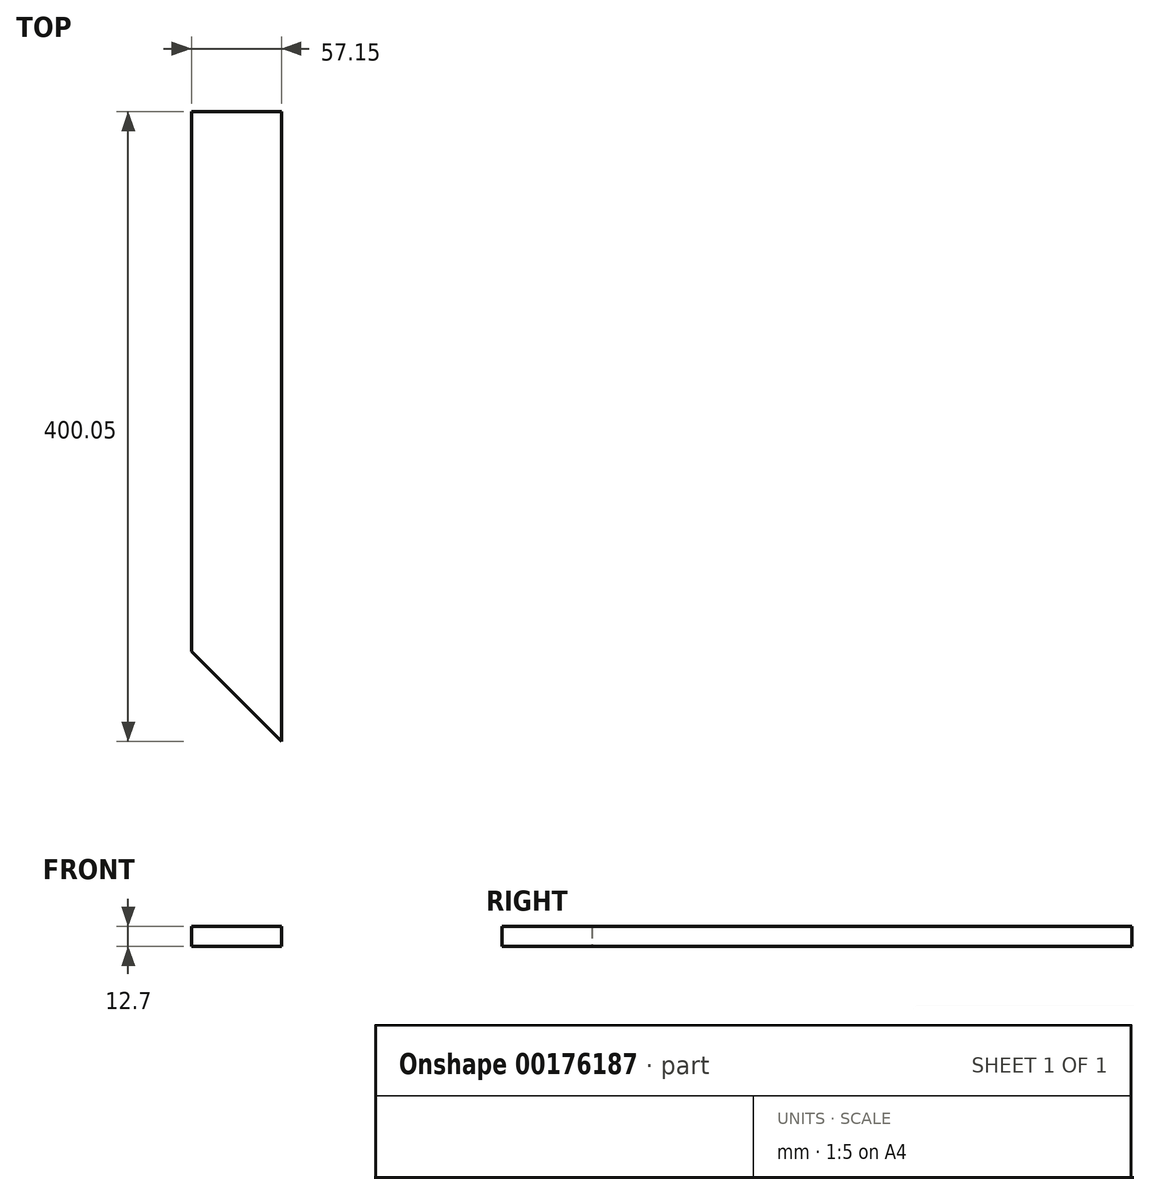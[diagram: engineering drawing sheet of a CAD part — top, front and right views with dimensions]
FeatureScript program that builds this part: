
annotation { "Feature Type Name" : "Feature", "Feature Type Description" : "" }
export const myFeature = defineFeature(function(context is Context, id is Id, definition is map)
    precondition{}
    {
        {
            var Q0;
            Q0=qCreatedBy(makeId("Top.planeOp"),FACE);
            var sketch = newSketch(context, id + "F0", { "sketchPlane" : qUnion([Q0])});
            skLineSegment(sketch, "E0", {"start": v(0, 57.15) * mm, "end": v(0, 400.05) * mm});
            skLineSegment(sketch, "E1", {"start": v(0, 400.05) * mm, "end": v(57.15, 400.05) * mm});
            skLineSegment(sketch, "E2", {"start": v(57.15, 400.05) * mm, "end": v(57.15, 0) * mm});
            skLineSegment(sketch, "E3", {"start": v(57.15, 0) * mm, "end": v(0, 57.15) * mm});
            skSolve(sketch);
        }
        {
            var Q0;
            Q0=makeQuery(id+"F0.imprint","IMPRINT",FACE,{"disambiguationData":[TD([[makeQuery(id+"F0.imprint","IMPRINT",EDGE,{"derivedFrom":sQuery(id+"F0.wireOp",EDGE,"E0")}),-1.0]])]});
            extrude(context, id + "F1", {"entities" : qUnion([Q0]), "depth" : 12.7 * mm});
        }
    });
